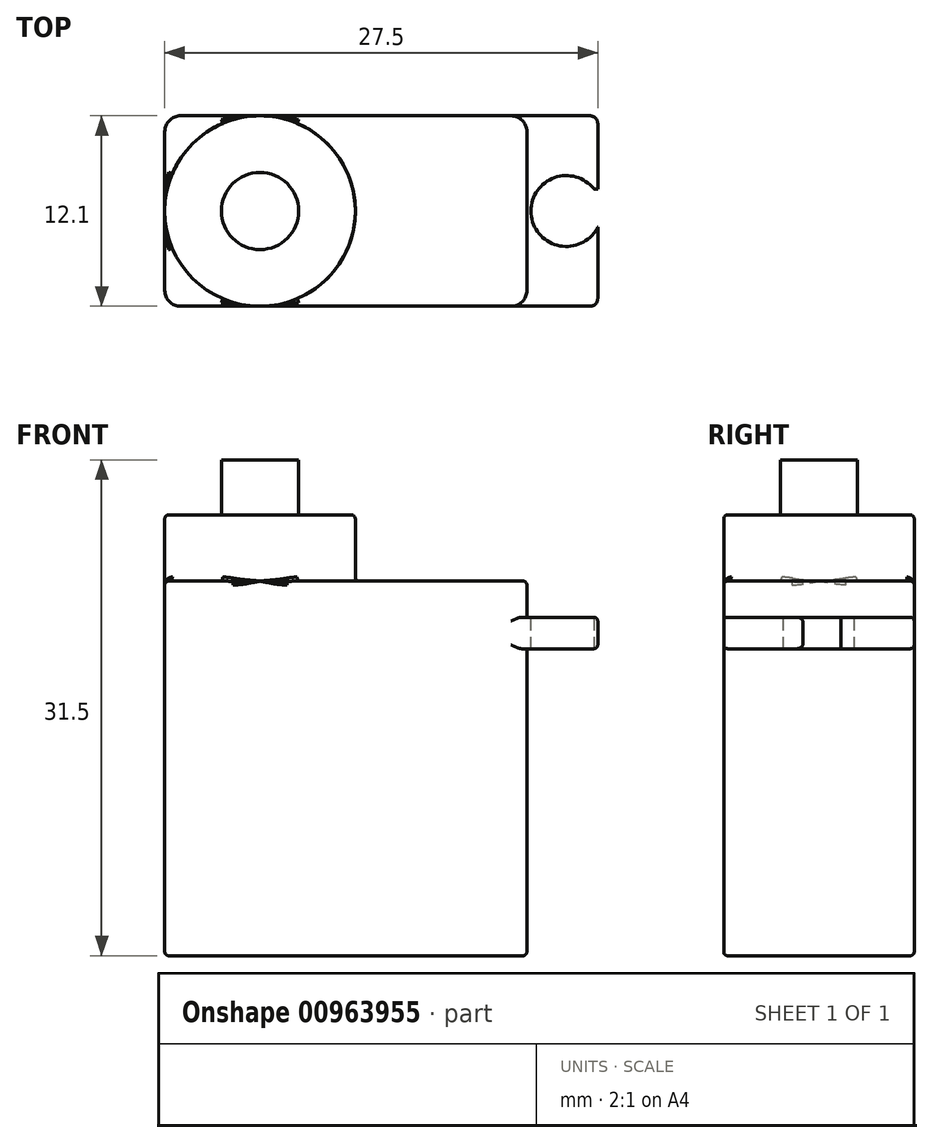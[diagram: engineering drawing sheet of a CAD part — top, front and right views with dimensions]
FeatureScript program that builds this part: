
annotation { "Feature Type Name" : "Feature", "Feature Type Description" : "" }
export const myFeature = defineFeature(function(context is Context, id is Id, definition is map)
    precondition{}
    {
        {
            var Q0;
            Q0=qCreatedBy(makeId("Top.planeOp"),FACE);
            var sketch = newSketch(context, id + "F0", { "sketchPlane" : qUnion([Q0])});
            skLineSegment(sketch, "E0.bottom", {"start": v(-11.5, 6.05) * mm, "end": v(11.5, 6.05) * mm});
            skLineSegment(sketch, "E0.top", {"start": v(-11.5, -6.05) * mm, "end": v(11.5, -6.05) * mm});
            skLineSegment(sketch, "E0.left", {"start": v(-11.5, 6.05) * mm, "end": v(-11.5, -6.05) * mm});
            skLineSegment(sketch, "E0.right", {"start": v(11.5, 6.05) * mm, "end": v(11.5, -6.05) * mm});
            skPoint(sketch, "E0.middle", {"position": v(0, 0) * mm});
            skSolve(sketch);
        }
        {
            var Q0;
            Q0 = qSketchRegion(id + "F0", true);
            extrude(context, id + "F1", {"entities" : qUnion([Q0]), "depth" : 23.8 * mm, "offsetDistance" : 25 * mm});
        }
        {
            var Q0;
            Q0=makeQuery(id+"F1.opExtrude","SWEPT_FACE",FACE,{"disambiguationData":[OSD([sQuery(id+"F0.wireOp",EDGE,"E0.right")])]});
            var sketch = newSketch(context, id + "F2", { "sketchPlane" : qUnion([Q0])});
            skLineSegment(sketch, "E1.bottom", {"start": v(-6.05, 21.5) * mm, "end": v(6.05, 21.5) * mm});
            skLineSegment(sketch, "E1.top", {"start": v(-6.05, 19.5) * mm, "end": v(6.05, 19.5) * mm});
            skLineSegment(sketch, "E1.left", {"start": v(-6.05, 21.5) * mm, "end": v(-6.05, 19.5) * mm});
            skLineSegment(sketch, "E1.right", {"start": v(6.05, 21.5) * mm, "end": v(6.05, 19.5) * mm});
            skPoint(sketch, "E1.middle", {"position": v(0, 20.5) * mm});
            skSolve(sketch);
        }
        {
            var Q0;
            Q0 = qSketchRegion(id + "F2", true);
            extrude(context, id + "F3", {"entities" : qUnion([Q0]), "operationType" : NewBodyOperationType.ADD, "depth" : 4.5 * mm, "offsetDistance" : 25 * mm});
        }
        {
            var Q0;
            Q0=makeQuery(id+"F3.opExtrude","SWEPT_FACE",FACE,{"disambiguationData":[OSD([sQuery(id+"F2.wireOp",EDGE,"E1.bottom")])]});
            var sketch = newSketch(context, id + "F4", { "sketchPlane" : qUnion([Q0])});
            skPoint(sketch, "E2", {"position": v(14, 0) * mm});
            skSolve(sketch);
        }
        {
            var Q0;
            Q0=sQuery(id+"F4.wireOp",VERTEX,"E2");
            var Q1;
            Q1=makeQuery(id+"F1.opExtrude","SWEPT_BODY",BODY,{"disambiguationData":[OSD([sQuery(id+"F0.wireOp",EDGE,"E0.bottom"),sQuery(id+"F0.wireOp",EDGE,"E0.top"),sQuery(id+"F0.wireOp",EDGE,"E0.left"),sQuery(id+"F0.wireOp",EDGE,"E0.right")])]});
            hole(context, id + "F5", {"style" : HoleStyle.SIMPLE, "endStyle" : HoleEndStyle.BLIND, "standardTappedOrClearance" : lookupTablePath({ "fit" : "Normal", "standard" : "ISO", "size" : "M4", "type" : "Clearance" }), "standardBlindInLast" : lookupTablePath({ "fit" : "Normal", "standard" : "ISO", "engagement" : "75%", "pitch" : "0.7 mm", "size" : "M4", "type" : "Clearance & tapped" }), "holeDiameter" : 4.5 * mm, "majorDiameter" : 5 * mm, "holeDepth" : 4 * mm, "isTappedThrough" : true, "tappedDepth" : 28.5 * mm, "tapClearance" : 3, "startFromSketch" : true, "locations" : qUnion([Q0]), "scope" : qUnion([Q1])});
        }
        {
            var Q0;
            Q0=makeQuery(id+"F3.opExtrude","SWEPT_FACE",FACE,{"disambiguationData":[OSD([sQuery(id+"F2.wireOp",EDGE,"E1.bottom")])]});
            var sketch = newSketch(context, id + "F6", { "sketchPlane" : qUnion([Q0])});
            skLineSegment(sketch, "E3.bottom", {"start": v(16, 1.03) * mm, "end": v(15.5, 1.03) * mm});
            skLineSegment(sketch, "E3.top", {"start": v(16, 1.38) * mm, "end": v(15.5, 1.38) * mm});
            skLineSegment(sketch, "E3.left", {"start": v(16, 1.03) * mm, "end": v(16, 1.38) * mm});
            skLineSegment(sketch, "E3.right", {"start": v(15.5, 1.03) * mm, "end": v(15.5, 1.38) * mm});
            skSolve(sketch);
        }
        {
            var Q0;
            Q0 = qSketchRegion(id + "F6", true);
            extrude(context, id + "F7", {"entities" : qUnion([Q0]), "operationType" : NewBodyOperationType.REMOVE, "oppositeDirection" : true, "depth" : 25 * mm, "offsetDistance" : 25 * mm});
        }
        {
            var Q0;
            Q0=makeQuery(id+"F1.opExtrude","CAP_FACE",FACE,{"disambiguationData":[OSD([sQuery(id+"F0.wireOp",EDGE,"E0.bottom"),sQuery(id+"F0.wireOp",EDGE,"E0.top"),sQuery(id+"F0.wireOp",EDGE,"E0.left"),sQuery(id+"F0.wireOp",EDGE,"E0.right")])],"isStart":false});
            var sketch = newSketch(context, id + "F8", { "sketchPlane" : qUnion([Q0])});
            skCircle(sketch, "E4", {"center": v(-5.45, 0) * mm, "radius": 6.05 * mm});
            skSolve(sketch);
        }
        {
            var Q0;
            Q0 = qSketchRegion(id + "F8", true);
            extrude(context, id + "F9", {"entities" : qUnion([Q0]), "operationType" : NewBodyOperationType.ADD, "depth" : 4.2 * mm, "offsetDistance" : 25 * mm});
        }
        {
            var Q0;
            Q0=makeQuery(id+"F9.opExtrude","CAP_FACE",FACE,{"disambiguationData":[OSD([sQuery(id+"F8.wireOp",EDGE,"E4")])],"isStart":false});
            var sketch = newSketch(context, id + "F10", { "sketchPlane" : qUnion([Q0])});
            skCircle(sketch, "E5", {"center": v(-5.45, 0) * mm, "radius": 2.45 * mm});
            skSolve(sketch);
        }
        {
            var Q0;
            Q0 = qSketchRegion(id + "F10", true);
            extrude(context, id + "F11", {"entities" : qUnion([Q0]), "depth" : 3.5 * mm, "offsetDistance" : 25 * mm});
        }
        {
            var Q0;
            Q0=makeQuery(id+"F1.opExtrude","SWEPT_EDGE",EDGE,{"disambiguationData":[OSD([sQuery(id+"F0.wireOp",EDGE,"E0.top"),sQuery(id+"F0.wireOp",EDGE,"E0.right")])]});
            var Q1;
            Q1=makeQuery(id+"F1.opExtrude","SWEPT_EDGE",EDGE,{"disambiguationData":[OSD([sQuery(id+"F0.wireOp",EDGE,"E0.bottom"),sQuery(id+"F0.wireOp",EDGE,"E0.right")])]});
            var Q2;
            Q2=makeQuery(id+"F1.opExtrude","SWEPT_EDGE",EDGE,{"disambiguationData":[OSD([sQuery(id+"F0.wireOp",EDGE,"E0.top"),sQuery(id+"F0.wireOp",EDGE,"E0.left")])]});
            var Q3;
            Q3=makeQuery(id+"F1.opExtrude","SWEPT_EDGE",EDGE,{"disambiguationData":[OSD([sQuery(id+"F0.wireOp",EDGE,"E0.bottom"),sQuery(id+"F0.wireOp",EDGE,"E0.left")])]});
            fillet(context, id + "F12", {"entities" : qUnion([Q0, Q1, Q2, Q3]), "radius" : 1 * mm, "tangentPropagation" : true, "allowEdgeOverflow" : false});
        }
        {
            var Q0;
            Q0=makeQuery(id+"FPBuGR0pm1aKetu_1.1.F3.opExtrude","CAP_EDGE",EDGE,{"disambiguationData":[OSD([sQuery(id+"F2.wireOp",EDGE,"E1.right")])],"isStart":false});
            var Q1;
            Q1=makeQuery(id+"FPBuGR0pm1aKetu_1.1.F3.opExtrude","CAP_EDGE",EDGE,{"disambiguationData":[OSD([sQuery(id+"F2.wireOp",EDGE,"E1.left")])],"isStart":false});
            var Q2;
            Q2=makeQuery(id+"F3.opExtrude","CAP_EDGE",EDGE,{"disambiguationData":[OSD([sQuery(id+"F2.wireOp",EDGE,"E1.right")])],"isStart":false});
            var Q3;
            Q3=makeQuery(id+"F3.opExtrude","CAP_EDGE",EDGE,{"disambiguationData":[OSD([sQuery(id+"F2.wireOp",EDGE,"E1.left")])],"isStart":false});
            fillet(context, id + "F13", {"entities" : qUnion([Q0, Q1, Q2, Q3]), "radius" : .5 * mm, "tangentPropagation" : true, "allowEdgeOverflow" : false});
        }
        {
            var Q0;
            Q0=makeQuery(id+"F1.opExtrude","CAP_FACE",FACE,{"disambiguationData":[OSD([sQuery(id+"F0.wireOp",EDGE,"E0.bottom"),sQuery(id+"F0.wireOp",EDGE,"E0.top"),sQuery(id+"F0.wireOp",EDGE,"E0.left"),sQuery(id+"F0.wireOp",EDGE,"E0.right")])],"isStart":true});
            var Q1;
            {var subQ0=sQuery(id+"F0.wireOp",EDGE,"E0.right");var subQ1=sQuery(id+"F0.wireOp",EDGE,"E0.top");Q1=makeQuery(id+"F9.boolean.opBoolean","SPLIT",EDGE,{"disambiguationData":[TD([makeQuery(id+"F1.opExtrude","SWEPT_FACE",FACE,{"disambiguationData":[OSD([subQ0])]})])],"derivedFrom":makeQuery(id+"F1.opExtrude","CAP_EDGE",EDGE,{"disambiguationData":[OSD([subQ1])],"isStart":false})});}
            var Q2;
            Q2=makeQuery(id+"F1.opExtrude","CAP_EDGE",EDGE,{"disambiguationData":[OSD([sQuery(id+"F0.wireOp",EDGE,"E0.right")])],"isStart":false});
            var Q3;
            {var subQ0=sQuery(id+"F0.wireOp",EDGE,"E0.bottom");var subQ1=sQuery(id+"F0.wireOp",EDGE,"E0.right");Q3=makeQuery(id+"F9.boolean.opBoolean","SPLIT",EDGE,{"disambiguationData":[TD([makeQuery(id+"F1.opExtrude","SWEPT_FACE",FACE,{"disambiguationData":[OSD([subQ1])]})])],"derivedFrom":makeQuery(id+"F1.opExtrude","CAP_EDGE",EDGE,{"disambiguationData":[OSD([subQ0])],"isStart":false})});}
            var Q4;
            Q4=makeQuery(id+"F3.opExtrude","SWEPT_EDGE",EDGE,{"disambiguationData":[OSD([sQuery(id+"F2.wireOp",EDGE,"E1.bottom"),sQuery(id+"F2.wireOp",EDGE,"E1.left")])]});
            var Q5;
            Q5=makeQuery(id+"F3.opExtrude","SWEPT_EDGE",EDGE,{"disambiguationData":[OSD([sQuery(id+"F2.wireOp",EDGE,"E1.bottom"),sQuery(id+"F2.wireOp",EDGE,"E1.right")])]});
            var Q6;
            Q6=makeQuery(id+"F3.opExtrude","SWEPT_EDGE",EDGE,{"disambiguationData":[OSD([sQuery(id+"F2.wireOp",EDGE,"E1.top"),sQuery(id+"F2.wireOp",EDGE,"E1.left")])]});
            var Q7;
            Q7=makeQuery(id+"F3.opExtrude","SWEPT_EDGE",EDGE,{"disambiguationData":[OSD([sQuery(id+"F2.wireOp",EDGE,"E1.top"),sQuery(id+"F2.wireOp",EDGE,"E1.right")])]});
            var Q8;
            Q8=makeQuery(id+"FPBuGR0pm1aKetu_1.1.F3.opExtrude","SWEPT_EDGE",EDGE,{"disambiguationData":[OSD([sQuery(id+"F2.wireOp",EDGE,"E1.bottom"),sQuery(id+"F2.wireOp",EDGE,"E1.left")])]});
            var Q9;
            Q9=makeQuery(id+"FPBuGR0pm1aKetu_1.1.F3.opExtrude","SWEPT_EDGE",EDGE,{"disambiguationData":[OSD([sQuery(id+"F2.wireOp",EDGE,"E1.bottom"),sQuery(id+"F2.wireOp",EDGE,"E1.right")])]});
            var Q10;
            Q10=makeQuery(id+"FPBuGR0pm1aKetu_1.1.F3.opExtrude","SWEPT_EDGE",EDGE,{"disambiguationData":[OSD([sQuery(id+"F2.wireOp",EDGE,"E1.top"),sQuery(id+"F2.wireOp",EDGE,"E1.left")])]});
            var Q11;
            Q11=makeQuery(id+"FPBuGR0pm1aKetu_1.1.F3.opExtrude","SWEPT_EDGE",EDGE,{"disambiguationData":[OSD([sQuery(id+"F2.wireOp",EDGE,"E1.top"),sQuery(id+"F2.wireOp",EDGE,"E1.right")])]});
            fillet(context, id + "F14", {"entities" : qUnion([Q0, Q1, Q2, Q3, Q4, Q5, Q6, Q7, Q8, Q9, Q10, Q11]), "radius" : .25 * mm, "tangentPropagation" : true, "allowEdgeOverflow" : false});
        }
        {
            var Q0;
            {var subQ0=sQuery(id+"F0.wireOp",EDGE,"E0.left");var subQ1=sQuery(id+"F0.wireOp",EDGE,"E0.top");var subQ2=sQuery(id+"F8.wireOp",EDGE,"E4");Q0=makeQuery(id+"F9.boolean.opBoolean","SPLIT",EDGE,{"disambiguationData":[TD([makeQuery(id+"F1.opExtrude","CAP_FACE",FACE,{"disambiguationData":[OSD([sQuery(id+"F0.wireOp",EDGE,"E0.bottom"),subQ1,subQ0,sQuery(id+"F0.wireOp",EDGE,"E0.right")])],"isStart":false}),makeQuery(id+"F1.opExtrude","SWEPT_FACE",FACE,{"disambiguationData":[OSD([subQ1])]}),makeQuery(id+"F1.opExtrude","SWEPT_FACE",FACE,{"disambiguationData":[OSD([subQ0])]}),makeQuery(id+"F9.opExtrude","SWEPT_FACE",FACE,{"disambiguationData":[OSD([subQ2])]})])],"derivedFrom":makeQuery(id+"F9.opExtrude","CAP_EDGE",EDGE,{"disambiguationData":[OSD([subQ2])],"isStart":true})});}
            var Q1;
            {var subQ0=sQuery(id+"F0.wireOp",EDGE,"E0.bottom");var subQ1=sQuery(id+"F0.wireOp",EDGE,"E0.top");var subQ2=sQuery(id+"F8.wireOp",EDGE,"E4");Q1=makeQuery(id+"F9.boolean.opBoolean","SPLIT",EDGE,{"disambiguationData":[TD([makeQuery(id+"F1.opExtrude","SWEPT_FACE",FACE,{"disambiguationData":[OSD([subQ0])]}),makeQuery(id+"F1.opExtrude","CAP_FACE",FACE,{"disambiguationData":[OSD([subQ0,subQ1,sQuery(id+"F0.wireOp",EDGE,"E0.left"),sQuery(id+"F0.wireOp",EDGE,"E0.right")])],"isStart":false}),makeQuery(id+"F1.opExtrude","SWEPT_FACE",FACE,{"disambiguationData":[OSD([subQ1])]}),makeQuery(id+"F9.opExtrude","SWEPT_FACE",FACE,{"disambiguationData":[OSD([subQ2])]})])],"derivedFrom":makeQuery(id+"F9.opExtrude","CAP_EDGE",EDGE,{"disambiguationData":[OSD([subQ2])],"isStart":true})});}
            var Q2;
            Q2=makeQuery(id+"F9.opExtrude","CAP_EDGE",EDGE,{"disambiguationData":[OSD([sQuery(id+"F8.wireOp",EDGE,"E4")])],"isStart":false});
            fillet(context, id + "F15", {"entities" : qUnion([Q0, Q1, Q2]), "radius" : .25 * mm, "tangentPropagation" : true, "allowEdgeOverflow" : false});
        }
    });
